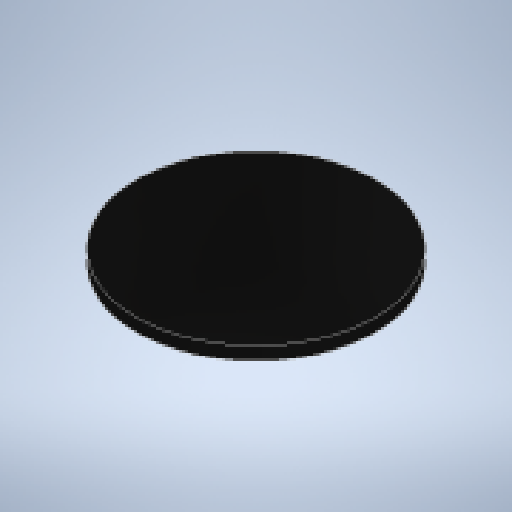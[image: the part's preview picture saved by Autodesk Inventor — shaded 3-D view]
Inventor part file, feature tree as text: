
AUTODESK INVENTOR PART (.ipt)
format: ipt  version: 2025.2 (Build 292293000, 293)  size: 219,136 bytes
history: native  units: mm
features: other x1, extrude x1, sketch x1
ambient origin geometry x8: Origin, YZ Plane, XZ Plane, XY Plane, X Axis, Y Axis, Z Axis, Center Point
bodies: Body1 (feature_tree)
feature tree (3):
  other  "ソリッド1"
  extrude  "押し出し1"  Depth=9.0mm
  sketch  "スケッチ1"
